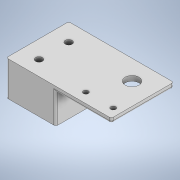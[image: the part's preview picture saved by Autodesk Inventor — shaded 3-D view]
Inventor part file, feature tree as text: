
AUTODESK INVENTOR PART (.ipt)
format: ipt  version: 2022.3 (Build 263350000, 350)  size: 163,328 bytes
history: native  units: in
note: dims shown in document units (in); Inventor stores cm internally (conversion verified against a paired STEP export)
features: extrude x5, sketch x5, fillet x1
ambient origin geometry x8: Origin, YZ Plane, XZ Plane, XY Plane, X Axis, Y Axis, Z Axis, Center Point
bodies: Solid1 (feature_tree)
feature tree (11):
  extrude  "Extrusion1"  Depth=2.65in
  extrude  "Extrusion2"  Depth=0.125in
  extrude  "Extrusion3"  Depth=1.25in
  extrude  "Extrusion6"  Depth=0.75in
  fillet  "Fillet1"  Radius=0.1719in
  extrude  "Extrusion7"  Depth=0.1in
  sketch  "Sketch1"  dims[d0=1.575in d1=2.65in]
  sketch  "Sketch2"  dims[d2=0.125in d3=0.0in d4=0.55in]
  sketch  "Sketch3"  dims[d6=0.25in d7=0.0in d8=1.25in]
  sketch  "Sketch6"  dims[d9=0.75in d10=0.0in d19=0.1719in d20=0.1719in]
  sketch  "Sketch7"  dims[d21=0.45in d22=0.45in d23=0.75in d24=0.375in d25=1.0in d26=0.0in d27=0.05in d28=0.5in d29=0.35in d30=0.125in d31=0.125in d32=0.2in d33=0.6929in d34=0.25in d35=0.25in d36=0.25in d37=0.6in d38=0.55in d39=0.1in d40=0.0in]
